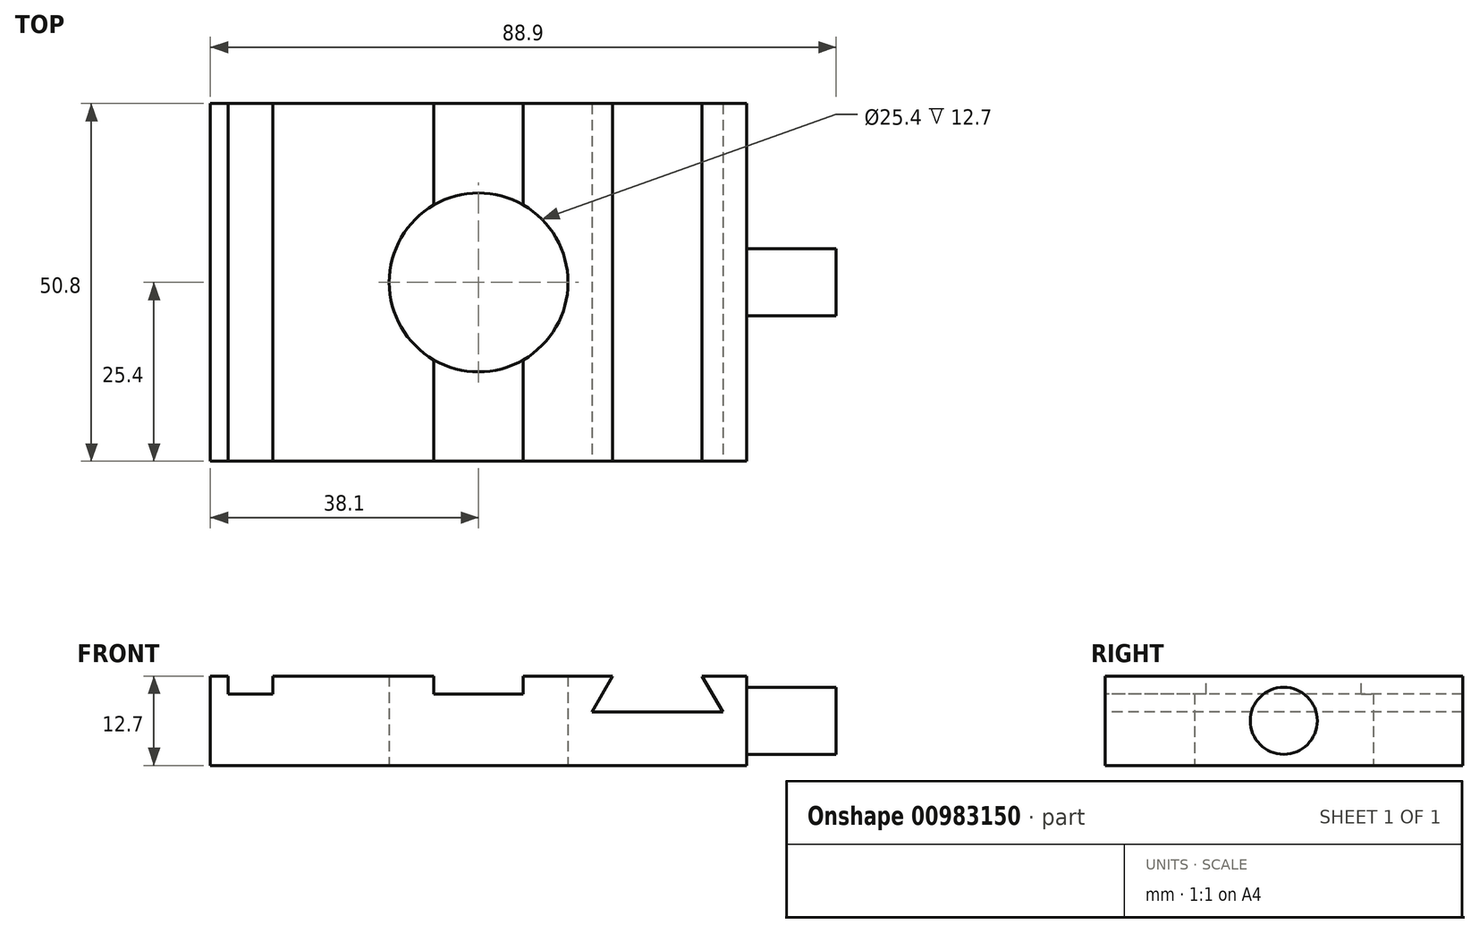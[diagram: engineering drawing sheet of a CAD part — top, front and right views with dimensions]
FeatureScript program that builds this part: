
annotation { "Feature Type Name" : "Feature", "Feature Type Description" : "" }
export const myFeature = defineFeature(function(context is Context, id is Id, definition is map)
    precondition{}
    {
        {
            var Q0;
            Q0=qCreatedBy(makeId("Top.planeOp"),FACE);
            var sketch = newSketch(context, id + "F0", { "sketchPlane" : qUnion([Q0])});
            skLineSegment(sketch, "E0.bottom", {"start": v(-38.1, 25.4) * mm, "end": v(38.1, 25.4) * mm});
            skLineSegment(sketch, "E0.top", {"start": v(-38.1, -25.4) * mm, "end": v(38.1, -25.4) * mm});
            skLineSegment(sketch, "E0.left", {"start": v(-38.1, 25.4) * mm, "end": v(-38.1, -25.4) * mm});
            skLineSegment(sketch, "E0.right", {"start": v(38.1, 25.4) * mm, "end": v(38.1, -25.4) * mm});
            skPoint(sketch, "E0.middle", {"position": v(0, 0) * mm});
            skCircle(sketch, "E1", {"center": v(0, 0) * mm, "radius": 12.7 * mm});
            skSolve(sketch);
        }
        {
            var Q0;
            Q0=makeQuery(id+"F0.imprint","IMPRINT",FACE,{"disambiguationData":[TD([[makeQuery(id+"F0.imprint","IMPRINT",EDGE,{"derivedFrom":sQuery(id+"F0.wireOp",EDGE,"E0.bottom")}),-1.0]])]});
            extrude(context, id + "F1", {"entities" : qUnion([Q0]), "depth" : 12.7 * mm, "offsetDistance" : 25.4 * mm});
        }
        {
            var Q0;
            Q0=makeQuery(id+"F1.opExtrude","CAP_FACE",FACE,{"disambiguationData":[OSD([sQuery(id+"F0.wireOp",EDGE,"E0.bottom"),sQuery(id+"F0.wireOp",EDGE,"E0.top"),sQuery(id+"F0.wireOp",EDGE,"E0.left"),sQuery(id+"F0.wireOp",EDGE,"E0.right"),sQuery(id+"F0.wireOp",EDGE,"E1")])],"isStart":false});
            var sketch = newSketch(context, id + "F2", { "sketchPlane" : qUnion([Q0])});
            skLineSegment(sketch, "E2.bottom", {"start": v(-35.56, 25.4) * mm, "end": v(-29.21, 25.4) * mm});
            skLineSegment(sketch, "E2.top", {"start": v(-35.56, -25.4) * mm, "end": v(-29.21, -25.4) * mm});
            skLineSegment(sketch, "E2.left", {"start": v(-35.56, 25.4) * mm, "end": v(-35.56, -25.4) * mm});
            skLineSegment(sketch, "E2.right", {"start": v(-29.21, 25.4) * mm, "end": v(-29.21, -25.4) * mm});
            skLineSegment(sketch, "E3", {"start": v(6.35, 25.4) * mm, "end": v(6.35, -25.4) * mm});
            skLineSegment(sketch, "E4", {"start": v(-6.35, 25.4) * mm, "end": v(-6.35, -25.4) * mm});
            skPoint(sketch, "E5", {"position": v(0, 0) * mm});
            skLineSegment(sketch, "E6", {"start": v(0, 25.4) * mm, "end": v(0, -25.4) * mm, "construction": true});
            skSolve(sketch);
        }
        {
            var Q0;
            Q0=makeQuery(id+"F2.imprint","IMPRINT",FACE,{"disambiguationData":[TD([[makeQuery(id+"F2.imprint","IMPRINT",EDGE,{"derivedFrom":sQuery(id+"F2.wireOp",EDGE,"E2.bottom")}),-1.0]])]});
            var Q1;
            {var subQ0=sQuery(id+"F2.wireOp",EDGE,"E3");var subQ1=makeQuery(id+"F1.opExtrude","CAP_EDGE",EDGE,{"disambiguationData":[OSD([sQuery(id+"F0.wireOp",EDGE,"E0.bottom")])],"isStart":false});var subQ2=makeQuery(id+"F2.imprint","INTERSECT",VERTEX,{"derivedFrom":[subQ1,subQ0]});Q1=makeQuery(id+"F2.imprint","IMPRINT",FACE,{"disambiguationData":[TD([[makeQuery(id+"F2.imprint","IMPRINT",EDGE,{"disambiguationData":[TD([[subQ2,-1.0]])],"derivedFrom":subQ0}),-1.0]])]});}
            var Q2;
            {var subQ0=sQuery(id+"F2.wireOp",EDGE,"E3");var subQ1=makeQuery(id+"F1.opExtrude","CAP_EDGE",EDGE,{"disambiguationData":[OSD([sQuery(id+"F0.wireOp",EDGE,"E0.top")])],"isStart":false});var subQ2=makeQuery(id+"F2.imprint","INTERSECT",VERTEX,{"derivedFrom":[subQ1,subQ0]});Q2=makeQuery(id+"F2.imprint","IMPRINT",FACE,{"disambiguationData":[TD([[makeQuery(id+"F2.imprint","IMPRINT",EDGE,{"disambiguationData":[TD([[subQ2,1.0]])],"derivedFrom":subQ0}),-1.0]])]});}
            extrude(context, id + "F3", {"entities" : qUnion([Q0, Q1, Q2]), "operationType" : NewBodyOperationType.REMOVE, "oppositeDirection" : true, "depth" : 2.54 * mm, "offsetDistance" : 25.4 * mm});
        }
        {
            var Q0;
            Q0=makeQuery(id+"F1.opExtrude","SWEPT_FACE",FACE,{"disambiguationData":[OSD([sQuery(id+"F0.wireOp",EDGE,"E0.top")])]});
            var sketch = newSketch(context, id + "F4", { "sketchPlane" : qUnion([Q0])});
            skLineSegment(sketch, "E7", {"start": v(19.05, 12.7) * mm, "end": v(16.12, 7.62) * mm});
            skLineSegment(sketch, "E8", {"start": v(16.12, 7.62) * mm, "end": v(34.68, 7.62) * mm});
            skLineSegment(sketch, "E9", {"start": v(34.68, 7.62) * mm, "end": v(31.75, 12.7) * mm});
            skLineSegment(sketch, "E10", {"start": v(31.75, 12.7) * mm, "end": v(19.05, 12.7) * mm});
            skLineSegment(sketch, "E11", {"start": v(25.4, 7.62) * mm, "end": v(25.4, 12.7) * mm, "construction": true});
            skSolve(sketch);
        }
        {
            var Q0;
            Q0=makeQuery(id+"F4.imprint","IMPRINT",FACE,{"disambiguationData":[TD([[makeQuery(id+"F4.imprint","IMPRINT",EDGE,{"derivedFrom":sQuery(id+"F4.wireOp",EDGE,"E7")}),1.0]])]});
            extrude(context, id + "F5", {"entities" : qUnion([Q0]), "operationType" : NewBodyOperationType.REMOVE, "endBound" : BoundingType.THROUGH_ALL, "oppositeDirection" : true, "depth" : 25.4 * mm, "offsetDistance" : 25.4 * mm});
        }
        {
            var Q0;
            Q0=makeQuery(id+"F1.opExtrude","SWEPT_FACE",FACE,{"disambiguationData":[OSD([sQuery(id+"F0.wireOp",EDGE,"E0.right")])]});
            var sketch = newSketch(context, id + "F6", { "sketchPlane" : qUnion([Q0])});
            skCircle(sketch, "E12", {"center": v(0, 6.35) * mm, "radius": 4.76 * mm});
            skPoint(sketch, "E12.centerSnap0", {"position": v(0, 12.7) * mm});
            skPoint(sketch, "E12.centerSnap1", {"position": v(-25.4, 6.35) * mm});
            skSolve(sketch);
        }
        {
            var Q0;
            Q0=makeQuery(id+"F6.imprint","IMPRINT",FACE,{"disambiguationData":[TD([[makeQuery(id+"F6.imprint","IMPRINT",EDGE,{"derivedFrom":sQuery(id+"F6.wireOp",EDGE,"E12")}),1.0]])]});
            extrude(context, id + "F7", {"entities" : qUnion([Q0]), "operationType" : NewBodyOperationType.ADD, "depth" : 12.7 * mm, "offsetDistance" : 25.4 * mm});
        }
    });
